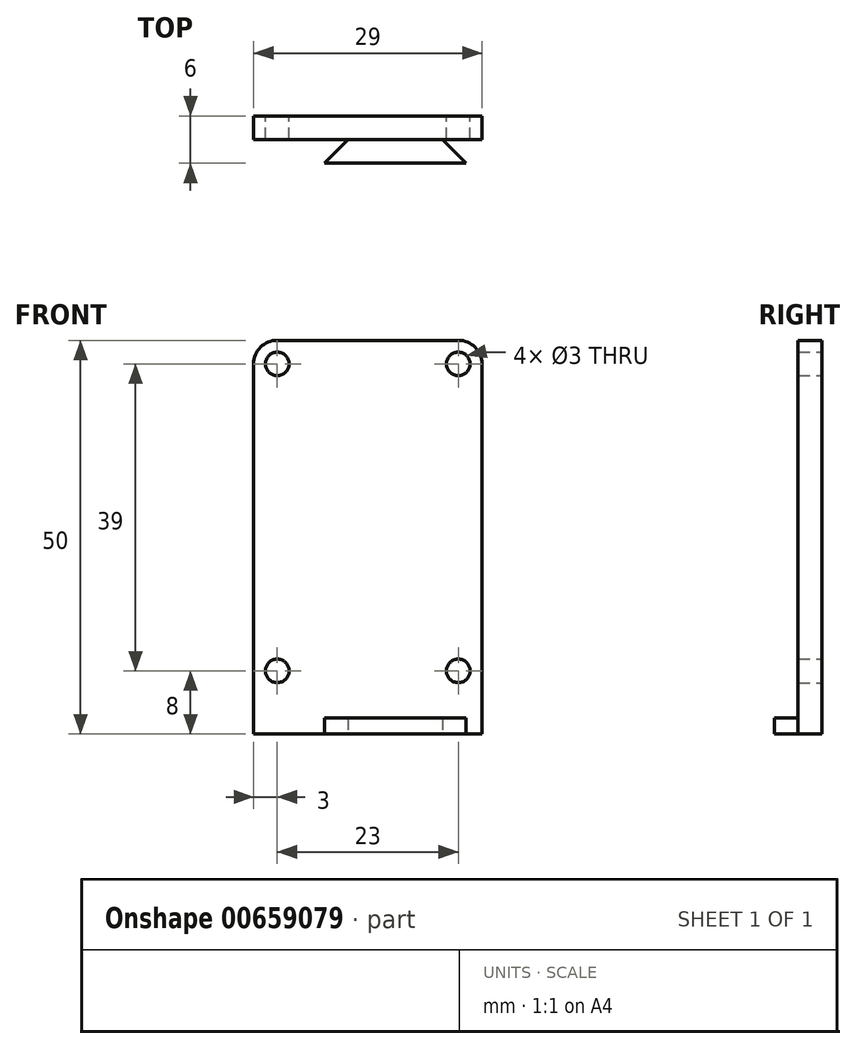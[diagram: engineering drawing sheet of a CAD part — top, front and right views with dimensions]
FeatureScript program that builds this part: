
annotation { "Feature Type Name" : "Feature", "Feature Type Description" : "" }
export const myFeature = defineFeature(function(context is Context, id is Id, definition is map)
    precondition{}
    {
        {
            var Q0;
            Q0=qCreatedBy(makeId("Top.planeOp"),FACE);
            var sketch = newSketch(context, id + "F0", { "sketchPlane" : qUnion([Q0])});
            skLineSegment(sketch, "E0", {"start": v(0, 0) * mm, "end": v(18, 0) * mm});
            skLineSegment(sketch, "E1", {"start": v(18, 0) * mm, "end": v(15, 3) * mm});
            skLineSegment(sketch, "E2", {"start": v(15, 3) * mm, "end": v(3, 3) * mm});
            skLineSegment(sketch, "E3", {"start": v(3, 3) * mm, "end": v(0, 0) * mm});
            skLineSegment(sketch, "E4.bottom", {"start": v(-9, 3) * mm, "end": v(20, 3) * mm});
            skLineSegment(sketch, "E4.top", {"start": v(-9, 6) * mm, "end": v(20, 6) * mm});
            skLineSegment(sketch, "E4.left", {"start": v(-9, 3) * mm, "end": v(-9, 6) * mm});
            skLineSegment(sketch, "E4.right", {"start": v(20, 3) * mm, "end": v(20, 6) * mm});
            skSolve(sketch);
        }
        {
            var Q0;
            Q0=makeQuery(id+"F0.imprint","IMPRINT",FACE,{"disambiguationData":[TD([[makeQuery(id+"F0.imprint","IMPRINT",EDGE,{"derivedFrom":sQuery(id+"F0.wireOp",EDGE,"E0")}),1.0]])]});
            extrude(context, id + "F1", {"entities" : qUnion([Q0]), "depth" : 2 * mm, "offsetDistance" : 25 * mm});
        }
        {
            var Q0;
            Q0=makeQuery(id+"F0.imprint","IMPRINT",FACE,{"disambiguationData":[TD([[makeQuery(id+"F0.imprint","IMPRINT",EDGE,{"derivedFrom":sQuery(id+"F0.wireOp",EDGE,"E4.top")}),-1.0]])]});
            extrude(context, id + "F2", {"entities" : qUnion([Q0]), "operationType" : NewBodyOperationType.ADD, "depth" : 50 * mm, "offsetDistance" : 25 * mm});
        }
        {
            var Q0;
            Q0=makeQuery(id+"F2.opExtrude","SWEPT_FACE",FACE,{"disambiguationData":[OSD([sQuery(id+"F0.wireOp",EDGE,"E4.top")])]});
            var sketch = newSketch(context, id + "F3", { "sketchPlane" : qUnion([Q0])});
            skCircle(sketch, "E5", {"center": v(6, 8) * mm, "radius": 1.5 * mm});
            skCircle(sketch, "E6", {"center": v(-17, 8) * mm, "radius": 1.5 * mm});
            skCircle(sketch, "E7", {"center": v(-17, 47) * mm, "radius": 1.5 * mm});
            skCircle(sketch, "E8", {"center": v(6, 47) * mm, "radius": 1.5 * mm});
            skSolve(sketch);
        }
        {
            var Q0;
            Q0=qSketchRegion(id+"F3",true);
            extrude(context, id + "F4", {"entities" : qUnion([Q0]), "operationType" : NewBodyOperationType.REMOVE, "oppositeDirection" : true, "depth" : 25 * mm, "offsetDistance" : 25 * mm});
        }
        {
            var Q0;
            Q0=makeQuery(id+"F2.opExtrude","CAP_EDGE",EDGE,{"disambiguationData":[OSD([sQuery(id+"F0.wireOp",EDGE,"E4.left")])],"isStart":false});
            var Q1;
            Q1=makeQuery(id+"F2.opExtrude","CAP_EDGE",EDGE,{"disambiguationData":[OSD([sQuery(id+"F0.wireOp",EDGE,"E4.right")])],"isStart":false});
            fillet(context, id + "F5", {"entities" : qUnion([Q0, Q1]), "radius" : 3 * mm, "tangentPropagation" : true, "allowEdgeOverflow" : false});
        }
    });
